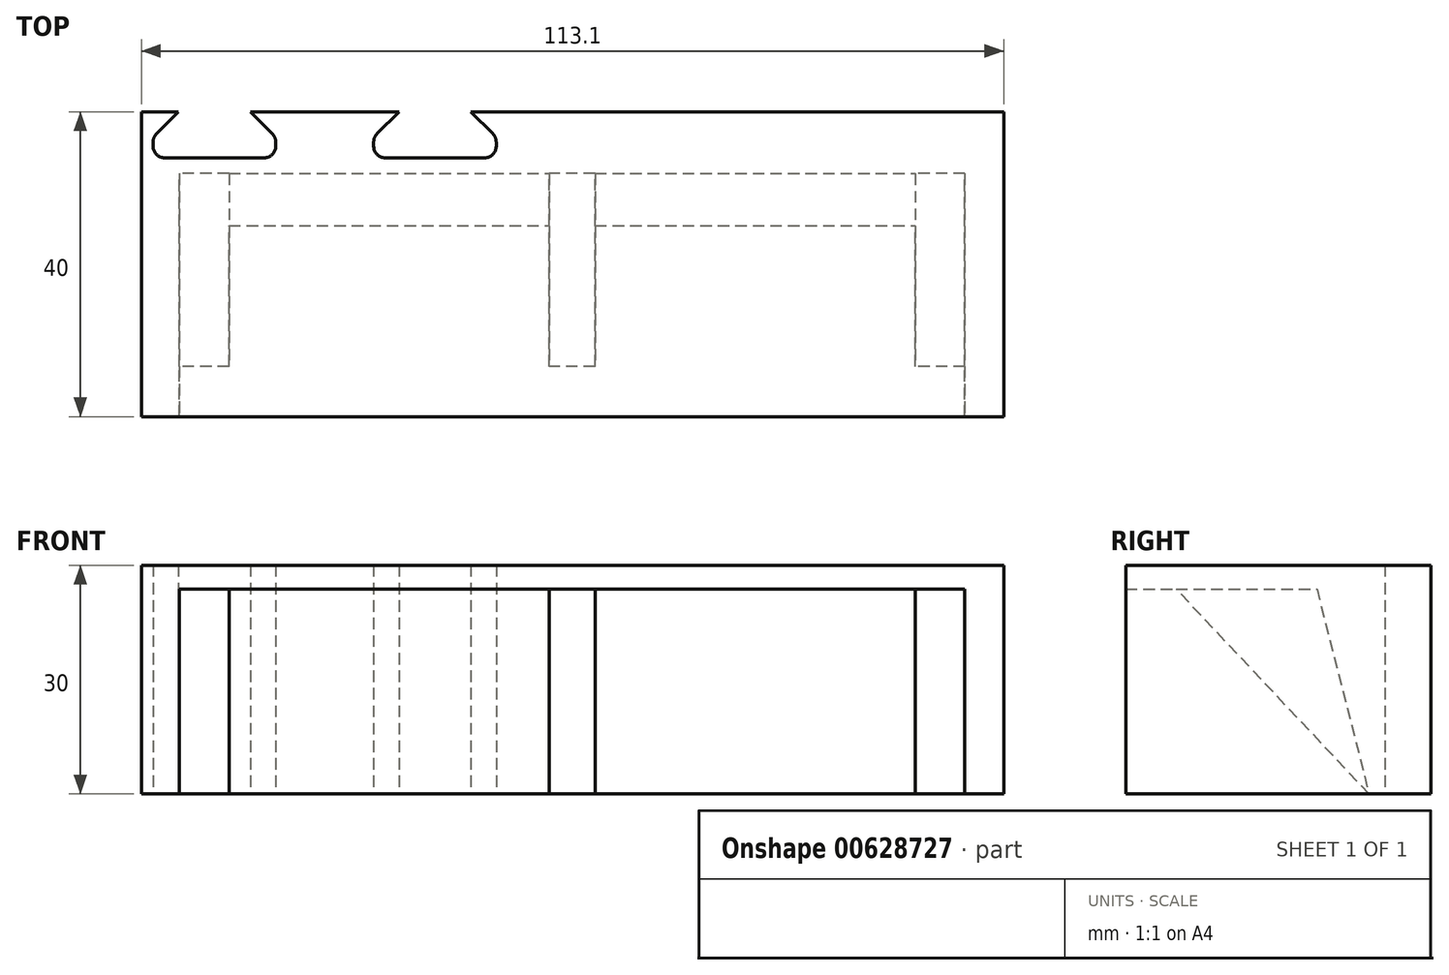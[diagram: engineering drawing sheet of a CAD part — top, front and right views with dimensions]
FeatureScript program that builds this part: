
annotation { "Feature Type Name" : "Feature", "Feature Type Description" : "" }
export const myFeature = defineFeature(function(context is Context, id is Id, definition is map)
    precondition{}
    {
        {
            var Q0;
            Q0=qCreatedBy(makeId("Top.planeOp"),FACE);
            var sketch = newSketch(context, id + "F0", { "sketchPlane" : qUnion([Q0])});
            skLineSegment(sketch, "E0.bottom", {"start": v(90, -35) * mm, "end": v(0, -35) * mm});
            skLineSegment(sketch, "E0.top", {"start": v(90, 35) * mm, "end": v(0, 35) * mm});
            skLineSegment(sketch, "E0.left", {"start": v(90, -35) * mm, "end": v(90, 35) * mm});
            skPoint(sketch, "E0.middle", {"position": v(0, 0) * mm});
            skPoint(sketch, "E1.middle", {"position": v(49.8, 0) * mm});
            skLineSegment(sketch, "E2", {"start": v(0, 0) * mm, "end": v(24, 0) * mm, "construction": true});
            skLineSegment(sketch, "E3", {"start": v(0, 0) * mm, "end": v(0, -14) * mm, "construction": true});
            skLineSegment(sketch, "E4", {"start": v(0, 0) * mm, "end": v(-35, 0) * mm, "construction": true});
            skLineSegment(sketch, "E5.bottom", {"start": v(-5, -19.5) * mm, "end": v(5, -19.5) * mm});
            skLineSegment(sketch, "E5.top", {"start": v(-5, 19.5) * mm, "end": v(5, 19.5) * mm});
            skLineSegment(sketch, "E5.left", {"start": v(-5, -19.5) * mm, "end": v(-5, 19.5) * mm});
            skLineSegment(sketch, "E5.right", {"start": v(5, -19.5) * mm, "end": v(5, 19.5) * mm});
            skLineSegment(sketch, "E6.bottom", {"start": v(-40, -17.25) * mm, "end": v(-30, -17.25) * mm});
            skLineSegment(sketch, "E6.top", {"start": v(-40, 17.25) * mm, "end": v(-30, 17.25) * mm});
            skLineSegment(sketch, "E6.left", {"start": v(-40, -17.25) * mm, "end": v(-40, 17.25) * mm});
            skLineSegment(sketch, "E6.right", {"start": v(-30, -17.25) * mm, "end": v(-30, 17.25) * mm});
            skPoint(sketch, "E6.middle", {"position": v(-35, 0) * mm});
            skLineSegment(sketch, "E7", {"start": v(0, 35) * mm, "end": v(0, 23) * mm});
            skPoint(sketch, "E7.endSnap0", {"position": v(0, 35) * mm});
            skLineSegment(sketch, "E8", {"start": v(0, 23) * mm, "end": v(-50, 23) * mm});
            skLineSegment(sketch, "E9", {"start": v(-50, 23) * mm, "end": v(-50, 0) * mm});
            skLineSegment(sketch, "E10.MirrorCS", {"start": v(-50, -23) * mm, "end": v(-50, 0) * mm});
            skLineSegment(sketch, "E11.MirrorCS", {"start": v(0, -35) * mm, "end": v(0, -23) * mm});
            skLineSegment(sketch, "E12.MirrorCS", {"start": v(0, -23) * mm, "end": v(-50, -23) * mm});
            skPoint(sketch, "E0.right.end.orphan", {"position": v(-90, 35) * mm});
            skPoint(sketch, "E13.orphan", {"position": v(-90, -35) * mm});
            skLineSegment(sketch, "E14.0", {"start": v(92.1, -37.1) * mm, "end": v(92.1, 37.1) * mm});
            skLineSegment(sketch, "E14.1", {"start": v(92.1, -37.1) * mm, "end": v(-2.1, -37.1) * mm});
            skLineSegment(sketch, "E14.2", {"start": v(92.1, 37.1) * mm, "end": v(-2.1, 37.1) * mm});
            skLineSegment(sketch, "E14.3", {"start": v(-2.1, -37.1) * mm, "end": v(-2.1, -25.1) * mm});
            skLineSegment(sketch, "E14.4", {"start": v(-2.1, -25.1) * mm, "end": v(-52.1, -25.1) * mm});
            skLineSegment(sketch, "E14.5", {"start": v(-2.1, 37.1) * mm, "end": v(-2.1, 25.1) * mm});
            skLineSegment(sketch, "E14.6", {"start": v(-2.1, 25.1) * mm, "end": v(-52.1, 25.1) * mm});
            skLineSegment(sketch, "E14.7", {"start": v(-52.1, 25.1) * mm, "end": v(-52.1, 0) * mm});
            skLineSegment(sketch, "E14.8", {"start": v(-52.1, -25.1) * mm, "end": v(-52.1, 0) * mm});
            skLineSegment(sketch, "E15.bottom", {"start": v(-30, 52.75) * mm, "end": v(-40, 52.75) * mm});
            skLineSegment(sketch, "E15.top", {"start": v(-30, 87.25) * mm, "end": v(-40, 87.25) * mm});
            skLineSegment(sketch, "E15.left", {"start": v(-30, 52.75) * mm, "end": v(-30, 87.25) * mm});
            skLineSegment(sketch, "E15.right", {"start": v(-40, 52.75) * mm, "end": v(-40, 87.25) * mm});
            skPoint(sketch, "E15.middle", {"position": v(-35, 70) * mm});
            skLineSegment(sketch, "E16.bottom", {"start": v(-5, 50.5) * mm, "end": v(5, 50.5) * mm});
            skLineSegment(sketch, "E16.top", {"start": v(-5, 89.5) * mm, "end": v(5, 89.5) * mm});
            skLineSegment(sketch, "E16.left", {"start": v(-5, 50.5) * mm, "end": v(-5, 89.5) * mm});
            skLineSegment(sketch, "E16.right", {"start": v(5, 50.5) * mm, "end": v(5, 89.5) * mm});
            skPoint(sketch, "E16.middle", {"position": v(0, 70) * mm});
            skPoint(sketch, "E16.middle.positionSnap0", {"position": v(-30, 70) * mm});
            skPoint(sketch, "E16.centerSnap0", {"position": v(-30, 70) * mm});
            skLineSegment(sketch, "E17", {"start": v(-35, 0) * mm, "end": v(-35, 70) * mm, "construction": true});
            skCircle(sketch, "E18", {"center": v(0, -14) * mm, "radius": 2 * mm});
            skLineSegment(sketch, "E19", {"start": v(-35, 0) * mm, "end": v(-35, -11.75) * mm, "construction": true});
            skCircle(sketch, "E20", {"center": v(-35, -11.75) * mm, "radius": 2 * mm});
            skCircle(sketch, "E21.MirrorC", {"center": v(-35, 11.75) * mm, "radius": 2 * mm});
            skCircle(sketch, "E22.MirrorC", {"center": v(0, 14) * mm, "radius": 2 * mm});
            skLineSegment(sketch, "E23", {"start": v(-35, 70) * mm, "end": v(-35, 81.75) * mm, "construction": true});
            skLineSegment(sketch, "E24", {"start": v(0, 70) * mm, "end": v(0, 84) * mm, "construction": true});
            skCircle(sketch, "E25", {"center": v(-35, 81.75) * mm, "radius": 2 * mm});
            skCircle(sketch, "E26", {"center": v(0, 84) * mm, "radius": 2 * mm});
            skLineSegment(sketch, "E27", {"start": v(-35, 70) * mm, "end": v(-30, 70) * mm, "construction": true});
            skCircle(sketch, "E28.MirrorC", {"center": v(-35, 58.25) * mm, "radius": 2 * mm});
            skCircle(sketch, "E29.MirrorC", {"center": v(0, 56) * mm, "radius": 2 * mm});
            skLineSegment(sketch, "E30", {"start": v(90, -35) * mm, "end": v(92.1, -35) * mm});
            skLineSegment(sketch, "E31", {"start": v(90, 35) * mm, "end": v(92.1, 35) * mm});
            skLineSegment(sketch, "E32", {"start": v(-2.1, 37.1) * mm, "end": v(-6.1, 37.1) * mm});
            skLineSegment(sketch, "E33", {"start": v(-6.1, 37.1) * mm, "end": v(-6.1, 25.1) * mm});
            skLineSegment(sketch, "E34", {"start": v(-2.1, -37.1) * mm, "end": v(-6.1, -37.1) * mm});
            skLineSegment(sketch, "E35", {"start": v(-6.1, -37.1) * mm, "end": v(-6.1, -25.1) * mm});
            skLineSegment(sketch, "E36", {"start": v(-41, 23) * mm, "end": v(-41, 11) * mm});
            skLineSegment(sketch, "E37", {"start": v(-41, 11) * mm, "end": v(-50, 11) * mm});
            skPoint(sketch, "E38.end.orphan", {"position": v(-41, 14.45) * mm});
            skLineSegment(sketch, "E39.MirrorCS", {"start": v(-41, -11) * mm, "end": v(-50, -11) * mm});
            skLineSegment(sketch, "E40.MirrorCS", {"start": v(-41, -23) * mm, "end": v(-41, -11) * mm});
            skLineSegment(sketch, "E41", {"start": v(90, -35) * mm, "end": v(90, -37.1) * mm});
            skLineSegment(sketch, "E42", {"start": v(90, 35) * mm, "end": v(90, 37.1) * mm});
            skLineSegment(sketch, "E43.bottom", {"start": v(90, 35) * mm, "end": v(86, 35) * mm});
            skLineSegment(sketch, "E43.left", {"start": v(90, 35) * mm, "end": v(90, 23) * mm});
            skLineSegment(sketch, "E44.bottom", {"start": v(90, -35) * mm, "end": v(86, -35) * mm});
            skLineSegment(sketch, "E44.left", {"start": v(90, -35) * mm, "end": v(90, -23) * mm});
            skLineSegment(sketch, "E45.bottom", {"start": v(86, -35) * mm, "end": v(80, -35) * mm});
            skLineSegment(sketch, "E46.bottom", {"start": v(86, 35) * mm, "end": v(80, 35) * mm});
            skLineSegment(sketch, "E47.bottom", {"start": v(0, 23) * mm, "end": v(7, 23) * mm});
            skLineSegment(sketch, "E47.top", {"start": v(0, 35) * mm, "end": v(12, 35) * mm});
            skLineSegment(sketch, "E47.left", {"start": v(0, 23) * mm, "end": v(0, 35) * mm});
            skLineSegment(sketch, "E47.right", {"start": v(12, 28) * mm, "end": v(12, 35) * mm});
            skLineSegment(sketch, "E48.bottom", {"start": v(0, -35) * mm, "end": v(12, -35) * mm});
            skLineSegment(sketch, "E48.top", {"start": v(0, -23) * mm, "end": v(7, -23) * mm});
            skLineSegment(sketch, "E48.right", {"start": v(12, -35) * mm, "end": v(12, -28) * mm});
            skCircle(sketch, "E49", {"center": v(6, -29) * mm, "radius": 2 * mm});
            skPoint(sketch, "E49.centerSnap0", {"position": v(6, -35) * mm});
            skPoint(sketch, "E49.centerSnap1", {"position": v(0, -29) * mm});
            skPoint(sketch, "E50.visualSharp", {"position": v(12, -23) * mm});
            skArc(sketch, "E50.filletArc", {"start": v(12, -28) * mm, "mid": v(10.54, -24.46) * mm, "end": v(7, -23) * mm});
            skPoint(sketch, "E51.visualSharp", {"position": v(12, 23) * mm});
            skArc(sketch, "E51.filletArc", {"start": v(7, 23) * mm, "mid": v(10.54, 24.46) * mm, "end": v(12, 28) * mm});
            skCircle(sketch, "E52.MirrorC", {"center": v(6, 29) * mm, "radius": 2 * mm});
            skCircle(sketch, "E53", {"center": v(6, 29) * mm, "radius": 4.5 * mm});
            skCircle(sketch, "E54.MirrorC", {"center": v(6, -29) * mm, "radius": 4.5 * mm});
            skCircle(sketch, "E55", {"center": v(0, 14) * mm, "radius": 6 * mm});
            skCircle(sketch, "E56", {"center": v(-35, 11.75) * mm, "radius": 6 * mm});
            skCircle(sketch, "E57", {"center": v(-35, -11.75) * mm, "radius": 6 * mm});
            skCircle(sketch, "E58", {"center": v(0, -14) * mm, "radius": 6 * mm});
            skLineSegment(sketch, "E59", {"start": v(-6.1, 25.1) * mm, "end": v(-6.08, 23) * mm});
            skLineSegment(sketch, "E60", {"start": v(-6.1, -25.1) * mm, "end": v(-6.1, -23) * mm});
            skLineSegment(sketch, "E61", {"start": v(-47.66, 23) * mm, "end": v(-47.66, 18) * mm, "construction": true});
            skLineSegment(sketch, "E62", {"start": v(-50, 18) * mm, "end": v(-45, 18) * mm, "construction": true});
            skCircle(sketch, "E63", {"center": v(-45, 18) * mm, "radius": 2.25 * mm});
            skCircle(sketch, "E64.MirrorC", {"center": v(-45, -18) * mm, "radius": 2.25 * mm});
            skCircle(sketch, "E65.MirrorC", {"center": v(-25, 18) * mm, "radius": 2.25 * mm});
            skCircle(sketch, "E66.MirrorC", {"center": v(-25, -18) * mm, "radius": 2.25 * mm});
            skCircle(sketch, "E67.MirrorC", {"center": v(28.54, -17.75) * mm, "radius": 2.25 * mm});
            skLineSegment(sketch, "E68.bottom", {"start": v(34.04, -22.75) * mm, "end": v(23.04, -22.75) * mm});
            skLineSegment(sketch, "E68.top", {"start": v(34.04, -12.75) * mm, "end": v(23.04, -12.75) * mm});
            skLineSegment(sketch, "E68.left", {"start": v(36.04, -20.75) * mm, "end": v(36.04, -14.75) * mm});
            skLineSegment(sketch, "E68.right", {"start": v(21.04, -20.75) * mm, "end": v(21.04, -14.75) * mm});
            skLineSegment(sketch, "E69.0", {"start": v(36.44, -12.35) * mm, "end": v(20.64, -12.35) * mm});
            skLineSegment(sketch, "E69.1", {"start": v(36.44, -23.15) * mm, "end": v(36.44, -12.35) * mm});
            skLineSegment(sketch, "E69.2", {"start": v(36.44, -23.15) * mm, "end": v(20.64, -23.15) * mm});
            skLineSegment(sketch, "E69.3", {"start": v(20.64, -23.15) * mm, "end": v(20.64, -12.35) * mm});
            skPoint(sketch, "E70.visualSharp", {"position": v(21.04, -12.75) * mm});
            skArc(sketch, "E70.filletArc", {"start": v(23.04, -12.75) * mm, "mid": v(21.62, -13.33) * mm, "end": v(21.04, -14.75) * mm});
            skPoint(sketch, "E71.visualSharp", {"position": v(36.04, -12.75) * mm});
            skArc(sketch, "E71.filletArc", {"start": v(36.04, -14.75) * mm, "mid": v(35.45, -13.33) * mm, "end": v(34.04, -12.75) * mm});
            skPoint(sketch, "E72.visualSharp", {"position": v(36.04, -22.75) * mm});
            skArc(sketch, "E72.filletArc", {"start": v(34.04, -22.75) * mm, "mid": v(35.45, -22.16) * mm, "end": v(36.04, -20.75) * mm});
            skPoint(sketch, "E73.visualSharp", {"position": v(21.04, -22.75) * mm});
            skArc(sketch, "E73.filletArc", {"start": v(21.04, -20.75) * mm, "mid": v(21.62, -22.16) * mm, "end": v(23.04, -22.75) * mm});
            skArc(sketch, "E74.0", {"start": v(39.54, -14.75) * mm, "mid": v(37.93, -10.86) * mm, "end": v(34.04, -9.25) * mm});
            skLineSegment(sketch, "E74.1", {"start": v(39.54, -20.75) * mm, "end": v(39.54, -14.75) * mm});
            skLineSegment(sketch, "E74.2", {"start": v(34.04, -9.25) * mm, "end": v(23.04, -9.25) * mm});
            skArc(sketch, "E74.3", {"start": v(34.04, -26.25) * mm, "mid": v(37.93, -24.64) * mm, "end": v(39.54, -20.75) * mm});
            skArc(sketch, "E74.4", {"start": v(23.04, -9.25) * mm, "mid": v(19.15, -10.86) * mm, "end": v(17.54, -14.75) * mm});
            skLineSegment(sketch, "E74.5", {"start": v(17.54, -20.75) * mm, "end": v(17.54, -14.75) * mm});
            skArc(sketch, "E74.6", {"start": v(17.54, -20.75) * mm, "mid": v(19.15, -24.64) * mm, "end": v(23.04, -26.25) * mm});
            skLineSegment(sketch, "E74.7", {"start": v(34.04, -26.25) * mm, "end": v(23.04, -26.25) * mm});
            skLineSegment(sketch, "E75", {"start": v(45, 37.1) * mm, "end": v(45, -37.1) * mm});
            skLineSegment(sketch, "E76", {"start": v(45, 31.57) * mm, "end": v(68, 31.57) * mm, "construction": true});
            skLineSegment(sketch, "E77", {"start": v(68, 35) * mm, "end": v(68, -35) * mm});
            skLineSegment(sketch, "E78", {"start": v(12, -28) * mm, "end": v(12, 28) * mm});
            skLineSegment(sketch, "E79", {"start": v(12, 35) * mm, "end": v(12, 37.1) * mm});
            skLineSegment(sketch, "E80", {"start": v(68, 35) * mm, "end": v(68, 37.1) * mm});
            skLineSegment(sketch, "E81", {"start": v(68, 31.57) * mm, "end": v(70.1, 31.57) * mm, "construction": true});
            skLineSegment(sketch, "E82", {"start": v(70.1, 37.1) * mm, "end": v(70.1, -37.1) * mm});
            skLineSegment(sketch, "E83", {"start": v(12, -35) * mm, "end": v(12, -37.1) * mm});
            skLineSegment(sketch, "E84", {"start": v(72.96, 0) * mm, "end": v(72.96, 17.5) * mm, "construction": true});
            skPoint(sketch, "E84.startSnap0", {"position": v(70.1, 0) * mm});
            skLineSegment(sketch, "E85", {"start": v(70.1, 13.5) * mm, "end": v(73.34, 10.26) * mm});
            skPoint(sketch, "E86.end.orphan", {"position": v(71.21, 13.5) * mm});
            skPoint(sketch, "E86.start.orphan", {"position": v(71.21, 17.5) * mm});
            skLineSegment(sketch, "E87", {"start": v(74.05, 9.96) * mm, "end": v(74.64, 9.96) * mm});
            skLineSegment(sketch, "E88", {"start": v(72.96, 17.5) * mm, "end": v(71.21, 17.5) * mm, "construction": true});
            skLineSegment(sketch, "E89.MirrorCS", {"start": v(70.1, 21.5) * mm, "end": v(73.34, 24.74) * mm});
            skLineSegment(sketch, "E90.MirrorCS", {"start": v(74.05, 25.04) * mm, "end": v(74.64, 25.04) * mm});
            skLineSegment(sketch, "E91", {"start": v(75.64, 24.04) * mm, "end": v(75.64, 10.96) * mm});
            skPoint(sketch, "E92.visualSharp", {"position": v(75.64, 25.04) * mm});
            skArc(sketch, "E92.filletArc", {"start": v(75.64, 24.04) * mm, "mid": v(75.34, 24.74) * mm, "end": v(74.64, 25.04) * mm});
            skPoint(sketch, "E93.visualSharp", {"position": v(73.64, 25.04) * mm});
            skArc(sketch, "E93.filletArc", {"start": v(74.05, 25.04) * mm, "mid": v(73.67, 24.96) * mm, "end": v(73.34, 24.74) * mm});
            skPoint(sketch, "E94.visualSharp", {"position": v(73.64, 9.96) * mm});
            skArc(sketch, "E94.filletArc", {"start": v(73.34, 10.26) * mm, "mid": v(73.67, 10.04) * mm, "end": v(74.05, 9.96) * mm});
            skPoint(sketch, "E95.visualSharp", {"position": v(75.64, 9.96) * mm});
            skArc(sketch, "E95.filletArc", {"start": v(74.64, 9.96) * mm, "mid": v(75.34, 10.26) * mm, "end": v(75.64, 10.96) * mm});
            skLineSegment(sketch, "E96.MirrorCS", {"start": v(70.1, -13.5) * mm, "end": v(73.34, -10.26) * mm});
            skArc(sketch, "E97.MirrorCS", {"start": v(73.34, -10.26) * mm, "mid": v(73.67, -10.04) * mm, "end": v(74.05, -9.96) * mm});
            skLineSegment(sketch, "E98.MirrorCS", {"start": v(74.05, -9.96) * mm, "end": v(74.64, -9.96) * mm});
            skArc(sketch, "E99.MirrorCS", {"start": v(74.64, -9.96) * mm, "mid": v(75.34, -10.26) * mm, "end": v(75.64, -10.96) * mm});
            skLineSegment(sketch, "E100.MirrorCS", {"start": v(75.64, -24.04) * mm, "end": v(75.64, -10.96) * mm});
            skLineSegment(sketch, "E101.MirrorCS", {"start": v(70.1, -21.5) * mm, "end": v(73.34, -24.74) * mm});
            skArc(sketch, "E102.MirrorCS", {"start": v(74.05, -25.04) * mm, "mid": v(73.67, -24.96) * mm, "end": v(73.34, -24.74) * mm});
            skLineSegment(sketch, "E103.MirrorCS", {"start": v(74.05, -25.04) * mm, "end": v(74.64, -25.04) * mm});
            skArc(sketch, "E104.MirrorCS", {"start": v(75.64, -24.04) * mm, "mid": v(75.34, -24.74) * mm, "end": v(74.64, -25.04) * mm});
            skLineSegment(sketch, "E105", {"start": v(68, -35) * mm, "end": v(56.64, -23.64) * mm, "construction": true});
            skArc(sketch, "E106.MirrorCS", {"start": v(43.26, -40.34) * mm, "mid": v(43.04, -40.67) * mm, "end": v(42.96, -41.05) * mm});
            skArc(sketch, "E107.MirrorCS", {"start": v(58.04, -41.05) * mm, "mid": v(57.96, -40.67) * mm, "end": v(57.74, -40.34) * mm});
            skArc(sketch, "E108.MirrorCS", {"start": v(42.96, -41.64) * mm, "mid": v(43.26, -42.34) * mm, "end": v(43.96, -42.64) * mm});
            skArc(sketch, "E109.MirrorCS", {"start": v(57.04, -42.64) * mm, "mid": v(57.74, -42.34) * mm, "end": v(58.04, -41.64) * mm});
            skLineSegment(sketch, "E110.MirrorCS", {"start": v(42.96, -41.05) * mm, "end": v(42.96, -41.64) * mm});
            skLineSegment(sketch, "E111.MirrorCS", {"start": v(58.04, -41.05) * mm, "end": v(58.04, -41.64) * mm});
            skLineSegment(sketch, "E112.MirrorCS", {"start": v(57.04, -42.64) * mm, "end": v(43.96, -42.64) * mm});
            skLineSegment(sketch, "E113.MirrorCS", {"start": v(46.5, -37.1) * mm, "end": v(43.26, -40.34) * mm});
            skLineSegment(sketch, "E114.MirrorCS", {"start": v(54.5, -37.1) * mm, "end": v(57.74, -40.34) * mm});
            skLineSegment(sketch, "E115", {"start": v(36.04, -37.1) * mm, "end": v(36.04, -40.15) * mm, "construction": true});
            skLineSegment(sketch, "E116.MirrorCS", {"start": v(14.04, -41.05) * mm, "end": v(14.04, -41.64) * mm});
            skArc(sketch, "E117.MirrorCS", {"start": v(14.04, -41.05) * mm, "mid": v(14.12, -40.67) * mm, "end": v(14.33, -40.34) * mm});
            skLineSegment(sketch, "E118.MirrorCS", {"start": v(29.11, -41.05) * mm, "end": v(29.11, -41.64) * mm});
            skArc(sketch, "E119.MirrorCS", {"start": v(28.82, -40.34) * mm, "mid": v(29.04, -40.67) * mm, "end": v(29.11, -41.05) * mm});
            skArc(sketch, "E120.MirrorCS", {"start": v(15.04, -42.64) * mm, "mid": v(14.33, -42.34) * mm, "end": v(14.04, -41.64) * mm});
            skLineSegment(sketch, "E121.MirrorCS", {"start": v(15.04, -42.64) * mm, "end": v(28.11, -42.64) * mm});
            skArc(sketch, "E122.MirrorCS", {"start": v(29.11, -41.64) * mm, "mid": v(28.82, -42.34) * mm, "end": v(28.11, -42.64) * mm});
            skLineSegment(sketch, "E123.MirrorCS", {"start": v(17.58, -37.1) * mm, "end": v(14.33, -40.34) * mm});
            skLineSegment(sketch, "E124.MirrorCS", {"start": v(25.58, -37.1) * mm, "end": v(28.82, -40.34) * mm});
            skLineSegment(sketch, "E125", {"start": v(28.54, -17.75) * mm, "end": v(28.54, 0) * mm, "construction": true});
            skLineSegment(sketch, "E126", {"start": v(28.54, 0) * mm, "end": v(56.04, 0) * mm, "construction": true});
            skLineSegment(sketch, "E127.bottom", {"start": v(53.54, 20) * mm, "end": v(58.54, 20) * mm});
            skLineSegment(sketch, "E127.top", {"start": v(53.54, -20) * mm, "end": v(58.54, -20) * mm});
            skLineSegment(sketch, "E127.left", {"start": v(53.54, 20) * mm, "end": v(53.54, -20) * mm});
            skLineSegment(sketch, "E127.right", {"start": v(58.54, 20) * mm, "end": v(58.54, -20) * mm});
            skPoint(sketch, "E127.middle", {"position": v(56.04, 0) * mm});
            skLineSegment(sketch, "E128", {"start": v(28.54, -17.75) * mm, "end": v(28.54, -35) * mm, "construction": true});
            skPoint(sketch, "E128.endSnap0", {"position": v(28.54, -26.25) * mm});
            skLineSegment(sketch, "E129", {"start": v(28.54, -17.75) * mm, "end": v(12, -17.75) * mm, "construction": true});
            skLineSegment(sketch, "E130", {"start": v(12, 17.54) * mm, "end": v(28.54, 17.54) * mm, "construction": true});
            skLineSegment(sketch, "E131", {"start": v(28.54, 17.54) * mm, "end": v(28.54, 35) * mm, "construction": true});
            skArc(sketch, "E132.MirrorCS", {"start": v(36.04, 14.75) * mm, "mid": v(35.45, 13.33) * mm, "end": v(34.04, 12.75) * mm});
            skArc(sketch, "E133.MirrorCS", {"start": v(23.04, 12.75) * mm, "mid": v(21.62, 13.33) * mm, "end": v(21.04, 14.75) * mm});
            skArc(sketch, "E134.MirrorCS", {"start": v(21.04, 20.75) * mm, "mid": v(21.62, 22.16) * mm, "end": v(23.04, 22.75) * mm});
            skArc(sketch, "E135.MirrorCS", {"start": v(34.04, 22.75) * mm, "mid": v(35.45, 22.16) * mm, "end": v(36.04, 20.75) * mm});
            skArc(sketch, "E136.MirrorCS", {"start": v(23.04, 9.25) * mm, "mid": v(19.15, 10.86) * mm, "end": v(17.54, 14.75) * mm});
            skLineSegment(sketch, "E137.MirrorCS", {"start": v(34.04, 9.25) * mm, "end": v(23.04, 9.25) * mm});
            skPoint(sketch, "E138.MirrorP", {"position": v(36.04, 12.75) * mm});
            skArc(sketch, "E139.MirrorCS", {"start": v(34.04, 26.25) * mm, "mid": v(37.93, 24.64) * mm, "end": v(39.54, 20.75) * mm});
            skArc(sketch, "E140.MirrorCS", {"start": v(17.54, 20.75) * mm, "mid": v(19.15, 24.64) * mm, "end": v(23.04, 26.25) * mm});
            skPoint(sketch, "E141.MirrorP", {"position": v(28.54, 17.75) * mm});
            skLineSegment(sketch, "E142.MirrorCS", {"start": v(36.44, 23.15) * mm, "end": v(20.64, 23.15) * mm});
            skPoint(sketch, "E143.MirrorP", {"position": v(21.04, 12.75) * mm});
            skLineSegment(sketch, "E144.MirrorCS", {"start": v(34.04, 26.25) * mm, "end": v(23.04, 26.25) * mm});
            skPoint(sketch, "E145.MirrorP", {"position": v(21.04, 22.75) * mm});
            skLineSegment(sketch, "E146.MirrorCS", {"start": v(20.64, 23.15) * mm, "end": v(20.64, 12.35) * mm});
            skLineSegment(sketch, "E147.MirrorCS", {"start": v(36.44, 12.35) * mm, "end": v(20.64, 12.35) * mm});
            skLineSegment(sketch, "E148.MirrorCS", {"start": v(17.54, 20.75) * mm, "end": v(17.54, 14.75) * mm});
            skCircle(sketch, "E149.MirrorC", {"center": v(28.54, 17.75) * mm, "radius": 2.25 * mm});
            skPoint(sketch, "E150.MirrorP", {"position": v(28.54, 26.25) * mm});
            skPoint(sketch, "E151.MirrorP", {"position": v(36.04, 22.75) * mm});
            skLineSegment(sketch, "E152.MirrorCS", {"start": v(21.04, 20.75) * mm, "end": v(21.04, 14.75) * mm});
            skLineSegment(sketch, "E153.MirrorCS", {"start": v(39.54, 20.75) * mm, "end": v(39.54, 14.75) * mm});
            skLineSegment(sketch, "E154.MirrorCS", {"start": v(36.44, 23.15) * mm, "end": v(36.44, 12.35) * mm});
            skLineSegment(sketch, "E155.MirrorCS", {"start": v(34.04, 22.75) * mm, "end": v(23.04, 22.75) * mm});
            skArc(sketch, "E156.MirrorCS", {"start": v(39.54, 14.75) * mm, "mid": v(37.93, 10.86) * mm, "end": v(34.04, 9.25) * mm});
            skLineSegment(sketch, "E157.MirrorCS", {"start": v(34.04, 12.75) * mm, "end": v(23.04, 12.75) * mm});
            skLineSegment(sketch, "E158.MirrorCS", {"start": v(36.04, 20.75) * mm, "end": v(36.04, 14.75) * mm});
            skArc(sketch, "E159.MirrorCS", {"start": v(29.11, 41.64) * mm, "mid": v(28.82, 42.34) * mm, "end": v(28.11, 42.64) * mm});
            skArc(sketch, "E160.MirrorCS", {"start": v(28.82, 40.34) * mm, "mid": v(29.04, 40.67) * mm, "end": v(29.11, 41.05) * mm});
            skArc(sketch, "E161.MirrorCS", {"start": v(15.04, 42.64) * mm, "mid": v(14.33, 42.34) * mm, "end": v(14.04, 41.64) * mm});
            skArc(sketch, "E162.MirrorCS", {"start": v(14.04, 41.05) * mm, "mid": v(14.12, 40.67) * mm, "end": v(14.33, 40.34) * mm});
            skArc(sketch, "E163.MirrorCS", {"start": v(57.04, 42.64) * mm, "mid": v(57.74, 42.34) * mm, "end": v(58.04, 41.64) * mm});
            skArc(sketch, "E164.MirrorCS", {"start": v(58.04, 41.05) * mm, "mid": v(57.96, 40.67) * mm, "end": v(57.74, 40.34) * mm});
            skLineSegment(sketch, "E165.MirrorCS", {"start": v(42.96, 41.05) * mm, "end": v(42.96, 41.64) * mm});
            skLineSegment(sketch, "E166.MirrorCS", {"start": v(58.04, 41.05) * mm, "end": v(58.04, 41.64) * mm});
            skLineSegment(sketch, "E167.MirrorCS", {"start": v(14.04, 41.05) * mm, "end": v(14.04, 41.64) * mm});
            skLineSegment(sketch, "E168.MirrorCS", {"start": v(29.11, 41.05) * mm, "end": v(29.11, 41.64) * mm});
            skArc(sketch, "E169.MirrorCS", {"start": v(42.96, 41.64) * mm, "mid": v(43.26, 42.34) * mm, "end": v(43.96, 42.64) * mm});
            skArc(sketch, "E170.MirrorCS", {"start": v(43.26, 40.34) * mm, "mid": v(43.04, 40.67) * mm, "end": v(42.96, 41.05) * mm});
            skLineSegment(sketch, "E171.MirrorCS", {"start": v(57.04, 42.64) * mm, "end": v(43.96, 42.64) * mm});
            skLineSegment(sketch, "E172.MirrorCS", {"start": v(15.04, 42.64) * mm, "end": v(28.11, 42.64) * mm});
            skLineSegment(sketch, "E173.MirrorCS", {"start": v(17.58, 37.1) * mm, "end": v(14.33, 40.34) * mm});
            skLineSegment(sketch, "E174.MirrorCS", {"start": v(25.58, 37.1) * mm, "end": v(28.82, 40.34) * mm});
            skLineSegment(sketch, "E175.MirrorCS", {"start": v(46.5, 37.1) * mm, "end": v(43.26, 40.34) * mm});
            skLineSegment(sketch, "E176.MirrorCS", {"start": v(54.5, 37.1) * mm, "end": v(57.74, 40.34) * mm});
            skLineSegment(sketch, "E177", {"start": v(92.1, 37.1) * mm, "end": v(125.1, 37.1) * mm});
            skLineSegment(sketch, "E178", {"start": v(125.1, 37.1) * mm, "end": v(125.1, -37.1) * mm});
            skLineSegment(sketch, "E179", {"start": v(125.1, -37.1) * mm, "end": v(92.1, -37.1) * mm});
            skLineSegment(sketch, "E180", {"start": v(125.1, 30.14) * mm, "end": v(123, 30.14) * mm, "construction": true});
            skLineSegment(sketch, "E181.0", {"start": v(70.1, 12.8) * mm, "end": v(72.99, 9.9) * mm});
            skArc(sketch, "E181.1", {"start": v(72.99, 9.9) * mm, "mid": v(73.48, 9.58) * mm, "end": v(74.05, 9.46) * mm});
            skLineSegment(sketch, "E181.2", {"start": v(74.05, 9.46) * mm, "end": v(74.64, 9.46) * mm});
            skArc(sketch, "E181.3", {"start": v(74.64, 9.46) * mm, "mid": v(75.7, 9.9) * mm, "end": v(76.14, 10.96) * mm});
            skLineSegment(sketch, "E181.4", {"start": v(76.14, 24.04) * mm, "end": v(76.14, 10.96) * mm});
            skLineSegment(sketch, "E181.5", {"start": v(70.1, 22.2) * mm, "end": v(72.99, 25.1) * mm});
            skArc(sketch, "E181.6", {"start": v(74.05, 25.54) * mm, "mid": v(73.48, 25.42) * mm, "end": v(72.99, 25.1) * mm});
            skLineSegment(sketch, "E181.7", {"start": v(74.05, 25.54) * mm, "end": v(74.64, 25.54) * mm});
            skArc(sketch, "E181.8", {"start": v(76.14, 24.04) * mm, "mid": v(75.7, 25.1) * mm, "end": v(74.64, 25.54) * mm});
            skLineSegment(sketch, "E182.MirrorCS", {"start": v(70.1, -12.8) * mm, "end": v(72.99, -9.9) * mm});
            skArc(sketch, "E183.MirrorCS", {"start": v(72.99, -9.9) * mm, "mid": v(73.48, -9.58) * mm, "end": v(74.05, -9.46) * mm});
            skLineSegment(sketch, "E184.MirrorCS", {"start": v(74.05, -9.46) * mm, "end": v(74.64, -9.46) * mm});
            skArc(sketch, "E185.MirrorCS", {"start": v(74.64, -9.46) * mm, "mid": v(75.7, -9.9) * mm, "end": v(76.14, -10.96) * mm});
            skLineSegment(sketch, "E186.MirrorCS", {"start": v(76.14, -24.04) * mm, "end": v(76.14, -10.96) * mm});
            skArc(sketch, "E187.MirrorCS", {"start": v(76.14, -24.04) * mm, "mid": v(75.7, -25.1) * mm, "end": v(74.64, -25.54) * mm});
            skLineSegment(sketch, "E188.MirrorCS", {"start": v(74.05, -25.54) * mm, "end": v(74.64, -25.54) * mm});
            skArc(sketch, "E189.MirrorCS", {"start": v(74.05, -25.54) * mm, "mid": v(73.48, -25.42) * mm, "end": v(72.99, -25.1) * mm});
            skLineSegment(sketch, "E190.MirrorCS", {"start": v(70.1, -22.2) * mm, "end": v(72.99, -25.1) * mm});
            skLineSegment(sketch, "E191.0", {"start": v(45.8, -37.1) * mm, "end": v(42.9, -39.99) * mm});
            skArc(sketch, "E191.1", {"start": v(42.9, -39.99) * mm, "mid": v(42.58, -40.48) * mm, "end": v(42.46, -41.05) * mm});
            skLineSegment(sketch, "E191.2", {"start": v(42.46, -41.05) * mm, "end": v(42.46, -41.64) * mm});
            skArc(sketch, "E191.3", {"start": v(42.46, -41.64) * mm, "mid": v(42.9, -42.7) * mm, "end": v(43.96, -43.14) * mm});
            skLineSegment(sketch, "E191.4", {"start": v(57.04, -43.14) * mm, "end": v(43.96, -43.14) * mm});
            skLineSegment(sketch, "E191.5", {"start": v(55.2, -37.1) * mm, "end": v(58.1, -39.99) * mm});
            skArc(sketch, "E191.6", {"start": v(58.54, -41.05) * mm, "mid": v(58.42, -40.48) * mm, "end": v(58.1, -39.99) * mm});
            skLineSegment(sketch, "E191.7", {"start": v(58.54, -41.05) * mm, "end": v(58.54, -41.64) * mm});
            skArc(sketch, "E191.8", {"start": v(57.04, -43.14) * mm, "mid": v(58.1, -42.7) * mm, "end": v(58.54, -41.64) * mm});
            skLineSegment(sketch, "E192.MirrorCS", {"start": v(26.28, -37.1) * mm, "end": v(29.17, -39.99) * mm});
            skArc(sketch, "E193.MirrorCS", {"start": v(29.17, -39.99) * mm, "mid": v(29.5, -40.48) * mm, "end": v(29.61, -41.05) * mm});
            skLineSegment(sketch, "E194.MirrorCS", {"start": v(29.61, -41.05) * mm, "end": v(29.61, -41.64) * mm});
            skArc(sketch, "E195.MirrorCS", {"start": v(29.61, -41.64) * mm, "mid": v(29.17, -42.7) * mm, "end": v(28.11, -43.14) * mm});
            skLineSegment(sketch, "E196.MirrorCS", {"start": v(15.04, -43.14) * mm, "end": v(28.11, -43.14) * mm});
            skArc(sketch, "E197.MirrorCS", {"start": v(15.04, -43.14) * mm, "mid": v(13.98, -42.7) * mm, "end": v(13.54, -41.64) * mm});
            skLineSegment(sketch, "E198.MirrorCS", {"start": v(13.54, -41.05) * mm, "end": v(13.54, -41.64) * mm});
            skArc(sketch, "E199.MirrorCS", {"start": v(13.54, -41.05) * mm, "mid": v(13.66, -40.48) * mm, "end": v(13.98, -39.99) * mm});
            skLineSegment(sketch, "E200.MirrorCS", {"start": v(16.87, -37.1) * mm, "end": v(13.98, -39.99) * mm});
            skLineSegment(sketch, "E201", {"start": v(12, -37.1) * mm, "end": v(12, -77.1) * mm});
            skLineSegment(sketch, "E202", {"start": v(12, -77.1) * mm, "end": v(125.1, -77.1) * mm});
            skLineSegment(sketch, "E203", {"start": v(125.1, -77.1) * mm, "end": v(125.1, -37.1) * mm});
            skSolve(sketch);
        }
        {
            var Q0;
            {var subQ9=sQuery(id+"F0.wireOp",EDGE,"E179");Q0=makeQuery(id+"F0.imprint","IMPRINT",FACE,{"disambiguationData":[TD([[makeQuery(id+"F0.imprint","IMPRINT",EDGE,{"derivedFrom":subQ9}),1.0]])]});}
            extrude(context, id + "F1", {"entities" : qUnion([Q0]), "depth" : 30 * mm});
        }
        {
            var Q0;
            Q0=qCreatedBy(makeId("Right.planeOp"),FACE);
            cPlane(context, id + "F2", {"entities" : qUnion([Q0]), "cplaneType" : CPlaneType.OFFSET, "offset" : 68.5 * mm, "width" : 150 * mm, "height" : 150 * mm});
        }
        {
            var Q0;
            Q0=qCreatedBy(id+"F2.planeOp",FACE);
            var sketch = newSketch(context, id + "F3", { "sketchPlane" : qUnion([Q0])});
            skLineSegment(sketch, "E204", {"start": v(0, 0) * mm, "end": v(-77.2, 0) * mm});
            skLineSegment(sketch, "E205", {"start": v(-77.2, 0) * mm, "end": v(-77.2, 26.9) * mm});
            skLineSegment(sketch, "E206", {"start": v(-77.2, 26.9) * mm, "end": v(-45.2, 26.9) * mm});
            skLineSegment(sketch, "E207", {"start": v(-45.2, 26.9) * mm, "end": v(-45.2, 0) * mm});
            skLineSegment(sketch, "E208", {"start": v(-45.2, 0) * mm, "end": v(-70.5, 26.9) * mm});
            skLineSegment(sketch, "E209", {"start": v(-45.2, 0) * mm, "end": v(-52.03, 26.9) * mm});
            skSolve(sketch);
        }
        {
            var Q0;
            Q0=qSketchRegion(id+"F3",true);
            extrude(context, id + "F4", {"entities" : qUnion([Q0]), "operationType" : NewBodyOperationType.REMOVE, "endBound" : BoundingType.SYMMETRIC, "depth" : 103 * mm});
        }
        {
            var Q0;
            {var subQ0=sQuery(id+"F3.wireOp",EDGE,"E207");Q0=makeQuery(id+"F3.imprint","IMPRINT",FACE,{"disambiguationData":[TD([[makeQuery(id+"F3.imprint","IMPRINT",EDGE,{"derivedFrom":subQ0}),-1.0]])]});}
            var Q1;
            {var subQ0=sQuery(id+"F3.wireOp",EDGE,"E208");Q1=makeQuery(id+"F3.imprint","IMPRINT",FACE,{"disambiguationData":[TD([[makeQuery(id+"F3.imprint","IMPRINT",EDGE,{"derivedFrom":subQ0}),-1.0]])]});}
            extrude(context, id + "F5", {"entities" : qUnion([Q0, Q1]), "operationType" : NewBodyOperationType.ADD, "endBound" : BoundingType.SYMMETRIC, "depth" : 107 * mm});
        }
        {
            var Q0;
            {var subQ0=sQuery(id+"F3.wireOp",EDGE,"E208");Q0=makeQuery(id+"F3.imprint","IMPRINT",FACE,{"disambiguationData":[TD([[makeQuery(id+"F3.imprint","IMPRINT",EDGE,{"derivedFrom":subQ0}),-1.0]])]});}
            extrude(context, id + "F6", {"entities" : qUnion([Q0]), "operationType" : NewBodyOperationType.REMOVE, "endBound" : BoundingType.SYMMETRIC, "oppositeDirection" : true, "depth" : 90 * mm});
        }
        {
            var Q0;
            {var subQ0=sQuery(id+"F3.wireOp",EDGE,"E207");Q0=makeQuery(id+"F3.imprint","IMPRINT",FACE,{"disambiguationData":[TD([[makeQuery(id+"F3.imprint","IMPRINT",EDGE,{"derivedFrom":subQ0}),-1.0]])]});}
            var Q1;
            {var subQ0=sQuery(id+"F3.wireOp",EDGE,"E208");Q1=makeQuery(id+"F3.imprint","IMPRINT",FACE,{"disambiguationData":[TD([[makeQuery(id+"F3.imprint","IMPRINT",EDGE,{"derivedFrom":subQ0}),-1.0]])]});}
            extrude(context, id + "F7", {"entities" : qUnion([Q0, Q1]), "operationType" : NewBodyOperationType.ADD, "endBound" : BoundingType.SYMMETRIC, "depth" : 6 * mm});
        }
    });
